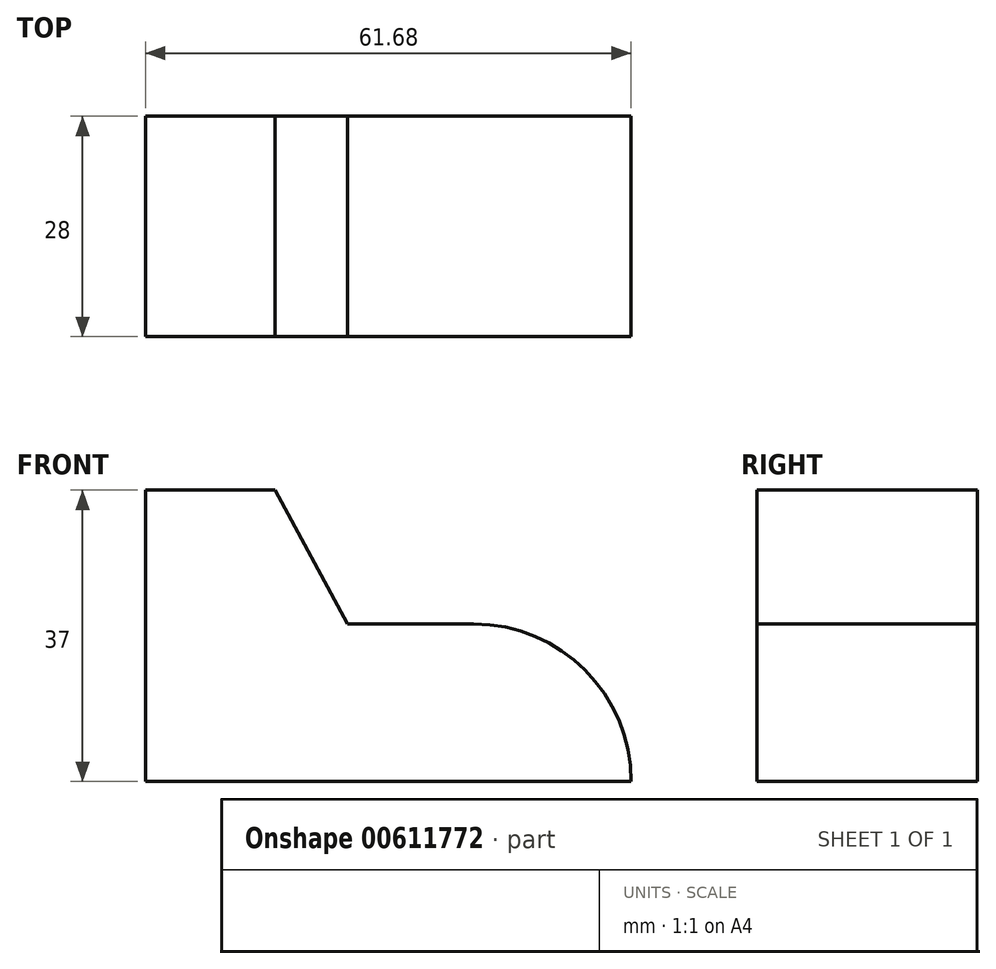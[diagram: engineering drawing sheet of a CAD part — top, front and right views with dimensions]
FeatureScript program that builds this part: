
annotation { "Feature Type Name" : "Feature", "Feature Type Description" : "" }
export const myFeature = defineFeature(function(context is Context, id is Id, definition is map)
    precondition{}
    {
        {
            var Q0;
            Q0=qCreatedBy(makeId("Front.planeOp"),FACE);
            var sketch = newSketch(context, id + "F0", { "sketchPlane" : qUnion([Q0])});
            skLineSegment(sketch, "E0.bottom", {"start": v(-9.2, 10.84) * mm, "end": v(7.23, 10.84) * mm});
            skLineSegment(sketch, "E0.left", {"start": v(-9.2, 10.84) * mm, "end": v(-9.2, -7.66) * mm});
            skLineSegment(sketch, "E1", {"start": v(16.48, -6.16) * mm, "end": v(7.23, 10.84) * mm});
            skLineSegment(sketch, "E2", {"start": v(16.48, -6.16) * mm, "end": v(32.48, -6.16) * mm});
            skLineSegment(sketch, "E3", {"start": v(52.48, -26.16) * mm, "end": v(52.48, -26.16) * mm});
            skLineSegment(sketch, "E4", {"start": v(52.48, -26.16) * mm, "end": v(-8.69, -26.16) * mm});
            skLineSegment(sketch, "E5", {"start": v(-9.2, -7.66) * mm, "end": v(-9.2, -26.16) * mm});
            skLineSegment(sketch, "E6", {"start": v(-9.2, -26.16) * mm, "end": v(-8.69, -26.16) * mm});
            skPoint(sketch, "E7.visualSharp", {"position": v(52.48, -6.16) * mm});
            skArc(sketch, "E7.filletArc", {"start": v(52.48, -26.16) * mm, "mid": v(46.62, -12.02) * mm, "end": v(32.48, -6.16) * mm});
            skSolve(sketch);
        }
        {
            var Q0;
            Q0 = qSketchRegion(id + "F0", true);
            extrude(context, id + "F1", {"entities" : qUnion([Q0]), "depth" : 28 * mm, "offsetDistance" : 25 * mm});
        }
    });
